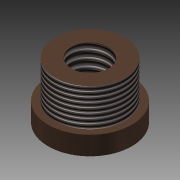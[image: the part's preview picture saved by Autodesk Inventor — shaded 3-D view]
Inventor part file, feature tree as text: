
AUTODESK INVENTOR PART (.ipt)
format: ipt  version: 2013 (Build 170138000, 138)  size: 103,424 bytes
history: native  units: in
note: dims shown in document units (in); Inventor stores cm internally (conversion verified against a paired STEP export)
features: extrude x3, sketch x3, thread x2
ambient origin geometry x8: Origin, YZ Plane, XZ Plane, XY Plane, X Axis, Y Axis, Z Axis, Center Point
bodies: Solid1 (feature_tree)
feature tree (8):
  extrude  "Extrusion1"  Depth=0.25in TaperAngle=0.0deg
  extrude  "Extrusion2"  Depth=0.5in TaperAngle=0.0deg
  extrude  "Extrusion3"  Depth=100.0in TaperAngle=0.0deg
  thread  "Thread1"  [1 undecoded]
  thread  "Thread2"  [1 undecoded]
  sketch  "Sketch1"  dims[d0=1.12in d1=0.25in d2=0.0in]
  sketch  "Sketch2"  dims[d3=0.937in d4=0.5in d5=0.0in]
  sketch  "Sketch3"  dims[d6=0.5in d7=100.0in d8=0.0in d9=1.0in d10=0.0in d11=1.0in d12=0.0in]
note: 2 required parameter values undecoded (feature->parameter linkage not recoverable at this tier; creation-order binding heuristic only, values carry confidence <= 0.55)
